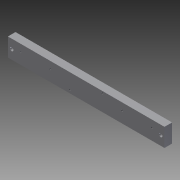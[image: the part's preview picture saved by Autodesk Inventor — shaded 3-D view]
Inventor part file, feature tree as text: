
AUTODESK INVENTOR PART (.ipt)
format: ipt  version: 2012 (Build 160160000, 160)  size: 93,184 bytes
history: native  units: in
note: dims shown in document units (in); Inventor stores cm internally (conversion verified against a paired STEP export)
features: reference x8, sketch x3, hole x2, extrude x1
ambient origin geometry x8: Origin, YZ Plane, XZ Plane, XY Plane, X Axis, Y Axis, Z Axis, Center Point
bodies: Solid1 (feature_tree)
feature tree (14):
  extrude  "Extrusion1"  Depth=7.7in
  hole  "Hole1"  [1 undecoded]
  hole  "Hole2"  [1 undecoded]
  sketch  "Sketch1"  dims[d0=0.9in d1=7.7in]
  sketch  "Sketch2"  dims[d2=0.375in d3=0.0in]
  reference  "Reference1"
  reference  "Reference2"
  sketch  "Sketch3"  dims[d4=0.17in d5=0.75in d6=0.332in d7=0.25in d8=0.5635in d9=1.0in d10=0.8108in d11=0.085in d12=0.75in d13=0.375in d14=0.06in d15=0.5635in d16=1.0in d17=0.8108in]
  reference  "Reference5"
  reference  "Reference6"
  reference  "Reference7"
  reference  "Reference8"
  reference  "Reference9"
  reference  "Reference10"
note: 2 required parameter values undecoded (feature->parameter linkage not recoverable at this tier; creation-order binding heuristic only, values carry confidence <= 0.55)
